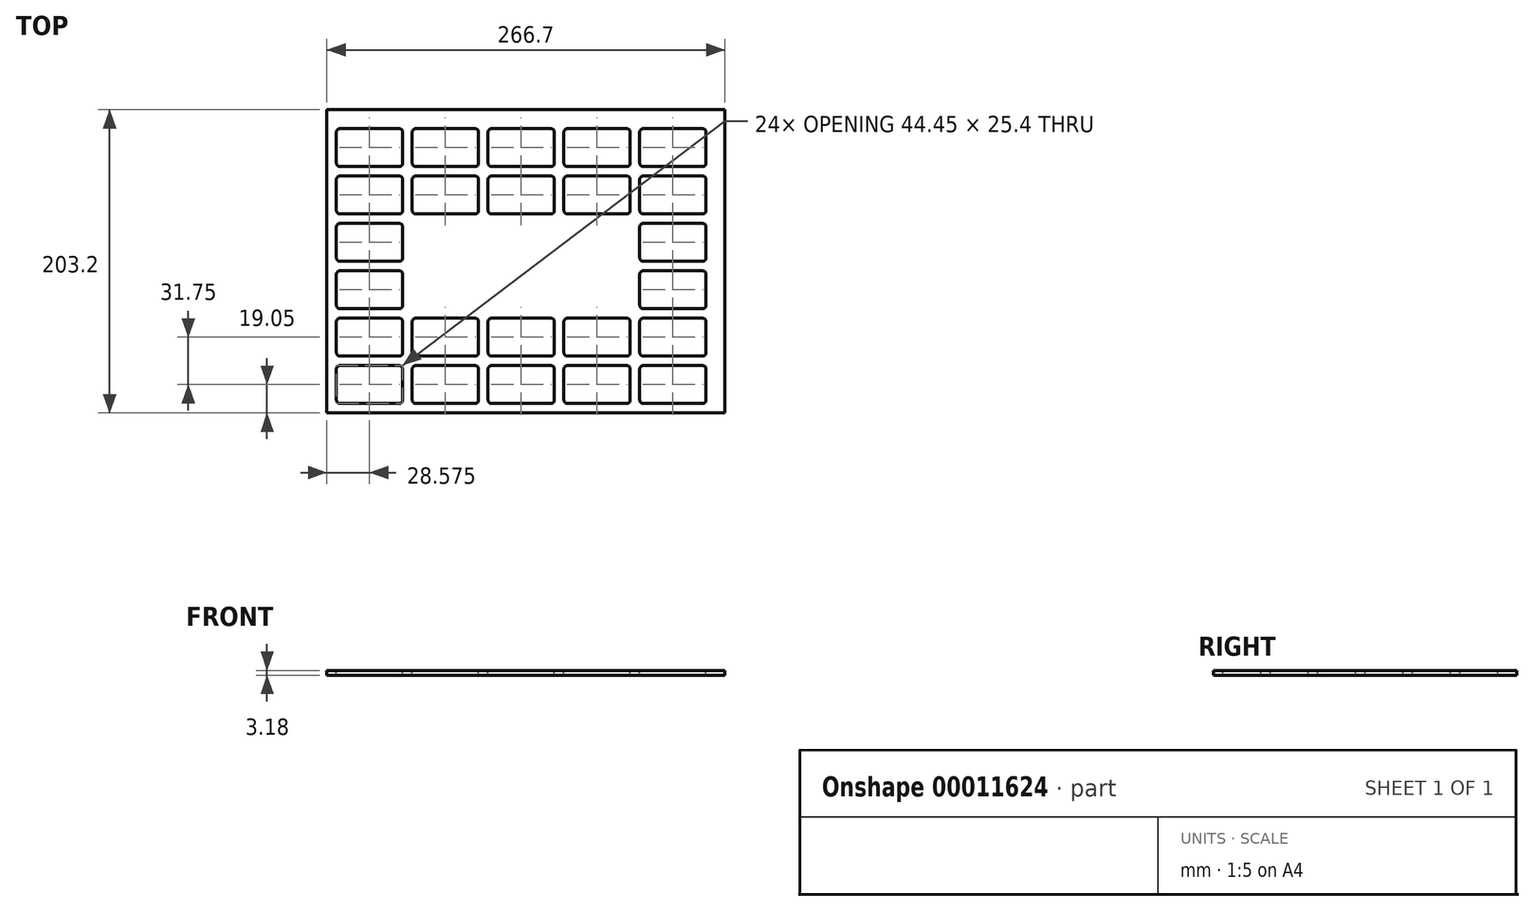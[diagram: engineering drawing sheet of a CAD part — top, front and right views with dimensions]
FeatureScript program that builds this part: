
annotation { "Feature Type Name" : "Feature", "Feature Type Description" : "" }
export const myFeature = defineFeature(function(context is Context, id is Id, definition is map)
    precondition{}
    {
        {
            var Q0;
            Q0=qCreatedBy(makeId("Top.planeOp"),FACE);
            var sketch = newSketch(context, id + "F0", { "sketchPlane" : qUnion([Q0])});
            skLineSegment(sketch, "E0.bottom", {"start": v(0, 0) * mm, "end": v(266.7, 0) * mm});
            skLineSegment(sketch, "E0.top", {"start": v(0, 203.2) * mm, "end": v(266.7, 203.2) * mm});
            skLineSegment(sketch, "E0.left", {"start": v(0, 0) * mm, "end": v(0, 203.2) * mm});
            skLineSegment(sketch, "E0.right", {"start": v(266.7, 0) * mm, "end": v(266.7, 203.2) * mm});
            skSolve(sketch);
        }
        {
            var Q0;
            Q0 = qSketchRegion(id + "F0", true);
            extrude(context, id + "F1", {"entities" : qUnion([Q0]), "oppositeDirection" : true, "depth" : 3.17 * mm});
        }
        {
            var Q0;
            Q0=makeQuery(id+"F0.imprint","IMPRINT",FACE,{"disambiguationData":[TD([[makeQuery(id+"F0.imprint","IMPRINT",EDGE,{"derivedFrom":sQuery(id+"F0.wireOp",EDGE,"E0.bottom")}),1.0]])]});
            var sketch = newSketch(context, id + "F2", { "sketchPlane" : qUnion([Q0])});
            skLineSegment(sketch, "E1.bottom", {"start": v(8.73, 6.35) * mm, "end": v(48.42, 6.35) * mm});
            skLineSegment(sketch, "E1.top", {"start": v(8.73, 31.75) * mm, "end": v(48.42, 31.75) * mm});
            skLineSegment(sketch, "E1.left", {"start": v(6.35, 8.73) * mm, "end": v(6.35, 29.37) * mm});
            skLineSegment(sketch, "E1.right", {"start": v(50.8, 8.73) * mm, "end": v(50.8, 29.37) * mm});
            skPoint(sketch, "E2.visualSharp", {"position": v(50.8, 31.75) * mm});
            skArc(sketch, "E2.filletArc", {"start": v(50.8, 29.37) * mm, "mid": v(50.1, 31.05) * mm, "end": v(48.42, 31.75) * mm});
            skPoint(sketch, "E3.visualSharp", {"position": v(50.8, 6.35) * mm});
            skArc(sketch, "E3.filletArc", {"start": v(48.42, 6.35) * mm, "mid": v(50.1, 7.05) * mm, "end": v(50.8, 8.73) * mm});
            skPoint(sketch, "E4.visualSharp", {"position": v(6.35, 6.35) * mm});
            skArc(sketch, "E4.filletArc", {"start": v(6.35, 8.73) * mm, "mid": v(7.05, 7.05) * mm, "end": v(8.73, 6.35) * mm});
            skPoint(sketch, "E5.visualSharp", {"position": v(6.35, 31.75) * mm});
            skArc(sketch, "E5.filletArc", {"start": v(8.73, 31.75) * mm, "mid": v(7.05, 31.05) * mm, "end": v(6.35, 29.37) * mm});
            skLineSegment(sketch, "E6.0.1.0", {"start": v(8.73, 63.5) * mm, "end": v(48.42, 63.5) * mm});
            skLineSegment(sketch, "E6.0.1.1", {"start": v(6.35, 40.48) * mm, "end": v(6.35, 61.12) * mm});
            skLineSegment(sketch, "E6.0.1.2", {"start": v(50.8, 40.48) * mm, "end": v(50.8, 61.12) * mm});
            skPoint(sketch, "E6.0.1.3", {"position": v(50.8, 63.5) * mm});
            skPoint(sketch, "E6.0.1.4", {"position": v(6.35, 38.1) * mm});
            skPoint(sketch, "E6.0.1.5", {"position": v(6.35, 63.5) * mm});
            skLineSegment(sketch, "E6.0.1.6", {"start": v(8.73, 38.1) * mm, "end": v(48.42, 38.1) * mm});
            skArc(sketch, "E6.0.1.7", {"start": v(6.35, 40.48) * mm, "mid": v(7.05, 38.8) * mm, "end": v(8.73, 38.1) * mm});
            skArc(sketch, "E6.0.1.8", {"start": v(8.73, 63.5) * mm, "mid": v(7.05, 62.8) * mm, "end": v(6.35, 61.12) * mm});
            skArc(sketch, "E6.0.1.9", {"start": v(50.8, 61.12) * mm, "mid": v(50.1, 62.8) * mm, "end": v(48.42, 63.5) * mm});
            skPoint(sketch, "E6.0.1.10", {"position": v(50.8, 38.1) * mm});
            skArc(sketch, "E6.0.1.11", {"start": v(48.42, 38.1) * mm, "mid": v(50.1, 38.8) * mm, "end": v(50.8, 40.48) * mm});
            skLineSegment(sketch, "E6.0.2.0", {"start": v(8.73, 95.25) * mm, "end": v(48.42, 95.25) * mm});
            skLineSegment(sketch, "E6.0.2.1", {"start": v(6.35, 72.23) * mm, "end": v(6.35, 92.87) * mm});
            skLineSegment(sketch, "E6.0.2.2", {"start": v(50.8, 72.23) * mm, "end": v(50.8, 92.87) * mm});
            skPoint(sketch, "E6.0.2.4", {"position": v(6.35, 69.85) * mm});
            skPoint(sketch, "E6.0.2.5", {"position": v(6.35, 95.25) * mm});
            skLineSegment(sketch, "E6.0.2.6", {"start": v(8.73, 69.85) * mm, "end": v(48.42, 69.85) * mm});
            skArc(sketch, "E6.0.2.7", {"start": v(6.35, 72.23) * mm, "mid": v(7.05, 70.55) * mm, "end": v(8.73, 69.85) * mm});
            skArc(sketch, "E6.0.2.8", {"start": v(8.73, 95.25) * mm, "mid": v(7.05, 94.55) * mm, "end": v(6.35, 92.87) * mm});
            skArc(sketch, "E6.0.2.9", {"start": v(50.8, 92.87) * mm, "mid": v(50.1, 94.55) * mm, "end": v(48.42, 95.25) * mm});
            skArc(sketch, "E6.0.2.11", {"start": v(48.42, 69.85) * mm, "mid": v(50.1, 70.55) * mm, "end": v(50.8, 72.23) * mm});
            skLineSegment(sketch, "E6.0.3.0", {"start": v(8.73, 127) * mm, "end": v(48.42, 127) * mm});
            skLineSegment(sketch, "E6.0.3.1", {"start": v(6.35, 103.98) * mm, "end": v(6.35, 124.62) * mm});
            skLineSegment(sketch, "E6.0.3.2", {"start": v(50.8, 103.98) * mm, "end": v(50.8, 124.62) * mm});
            skPoint(sketch, "E6.0.3.4", {"position": v(6.35, 101.6) * mm});
            skPoint(sketch, "E6.0.3.5", {"position": v(6.35, 127) * mm});
            skLineSegment(sketch, "E6.0.3.6", {"start": v(8.73, 101.6) * mm, "end": v(48.42, 101.6) * mm});
            skArc(sketch, "E6.0.3.7", {"start": v(6.35, 103.98) * mm, "mid": v(7.05, 102.3) * mm, "end": v(8.73, 101.6) * mm});
            skArc(sketch, "E6.0.3.8", {"start": v(8.73, 127) * mm, "mid": v(7.05, 126.3) * mm, "end": v(6.35, 124.62) * mm});
            skArc(sketch, "E6.0.3.9", {"start": v(50.8, 124.62) * mm, "mid": v(50.1, 126.3) * mm, "end": v(48.42, 127) * mm});
            skArc(sketch, "E6.0.3.11", {"start": v(48.42, 101.6) * mm, "mid": v(50.1, 102.3) * mm, "end": v(50.8, 103.98) * mm});
            skLineSegment(sketch, "E6.0.4.0", {"start": v(8.73, 158.75) * mm, "end": v(48.42, 158.75) * mm});
            skLineSegment(sketch, "E6.0.4.1", {"start": v(6.35, 135.73) * mm, "end": v(6.35, 156.37) * mm});
            skLineSegment(sketch, "E6.0.4.2", {"start": v(50.8, 135.73) * mm, "end": v(50.8, 156.37) * mm});
            skPoint(sketch, "E6.0.4.3", {"position": v(50.8, 158.75) * mm});
            skPoint(sketch, "E6.0.4.4", {"position": v(6.35, 133.35) * mm});
            skPoint(sketch, "E6.0.4.5", {"position": v(6.35, 158.75) * mm});
            skLineSegment(sketch, "E6.0.4.6", {"start": v(8.73, 133.35) * mm, "end": v(48.42, 133.35) * mm});
            skArc(sketch, "E6.0.4.7", {"start": v(6.35, 135.73) * mm, "mid": v(7.05, 134.05) * mm, "end": v(8.73, 133.35) * mm});
            skArc(sketch, "E6.0.4.8", {"start": v(8.73, 158.75) * mm, "mid": v(7.05, 158.05) * mm, "end": v(6.35, 156.37) * mm});
            skArc(sketch, "E6.0.4.9", {"start": v(50.8, 156.37) * mm, "mid": v(50.1, 158.05) * mm, "end": v(48.42, 158.75) * mm});
            skArc(sketch, "E6.0.4.11", {"start": v(48.42, 133.35) * mm, "mid": v(50.1, 134.05) * mm, "end": v(50.8, 135.73) * mm});
            skLineSegment(sketch, "E6.0.5.0", {"start": v(8.73, 190.5) * mm, "end": v(48.42, 190.5) * mm});
            skLineSegment(sketch, "E6.0.5.1", {"start": v(6.35, 167.48) * mm, "end": v(6.35, 188.12) * mm});
            skLineSegment(sketch, "E6.0.5.2", {"start": v(50.8, 167.48) * mm, "end": v(50.8, 188.12) * mm});
            skPoint(sketch, "E6.0.5.3", {"position": v(50.8, 190.5) * mm});
            skPoint(sketch, "E6.0.5.4", {"position": v(6.35, 165.1) * mm});
            skPoint(sketch, "E6.0.5.5", {"position": v(6.35, 190.5) * mm});
            skLineSegment(sketch, "E6.0.5.6", {"start": v(8.73, 165.1) * mm, "end": v(48.42, 165.1) * mm});
            skArc(sketch, "E6.0.5.7", {"start": v(6.35, 167.48) * mm, "mid": v(7.05, 165.8) * mm, "end": v(8.73, 165.1) * mm});
            skArc(sketch, "E6.0.5.8", {"start": v(8.73, 190.5) * mm, "mid": v(7.05, 189.8) * mm, "end": v(6.35, 188.12) * mm});
            skArc(sketch, "E6.0.5.9", {"start": v(50.8, 188.12) * mm, "mid": v(50.1, 189.8) * mm, "end": v(48.42, 190.5) * mm});
            skPoint(sketch, "E6.0.5.10", {"position": v(50.8, 165.1) * mm});
            skArc(sketch, "E6.0.5.11", {"start": v(48.42, 165.1) * mm, "mid": v(50.1, 165.8) * mm, "end": v(50.8, 167.48) * mm});
            skLineSegment(sketch, "E6.1.0.0", {"start": v(59.53, 31.75) * mm, "end": v(99.22, 31.75) * mm});
            skLineSegment(sketch, "E6.1.0.1", {"start": v(57.15, 8.73) * mm, "end": v(57.15, 29.37) * mm});
            skLineSegment(sketch, "E6.1.0.2", {"start": v(101.6, 8.73) * mm, "end": v(101.6, 29.37) * mm});
            skPoint(sketch, "E6.1.0.3", {"position": v(101.6, 31.75) * mm});
            skPoint(sketch, "E6.1.0.4", {"position": v(57.15, 6.35) * mm});
            skPoint(sketch, "E6.1.0.5", {"position": v(57.15, 31.75) * mm});
            skLineSegment(sketch, "E6.1.0.6", {"start": v(59.53, 6.35) * mm, "end": v(99.22, 6.35) * mm});
            skArc(sketch, "E6.1.0.7", {"start": v(57.15, 8.73) * mm, "mid": v(57.85, 7.05) * mm, "end": v(59.53, 6.35) * mm});
            skArc(sketch, "E6.1.0.8", {"start": v(59.53, 31.75) * mm, "mid": v(57.85, 31.05) * mm, "end": v(57.15, 29.37) * mm});
            skArc(sketch, "E6.1.0.9", {"start": v(101.6, 29.37) * mm, "mid": v(100.9, 31.05) * mm, "end": v(99.22, 31.75) * mm});
            skPoint(sketch, "E6.1.0.10", {"position": v(101.6, 6.35) * mm});
            skArc(sketch, "E6.1.0.11", {"start": v(99.22, 6.35) * mm, "mid": v(100.9, 7.05) * mm, "end": v(101.6, 8.73) * mm});
            skLineSegment(sketch, "E6.1.1.0", {"start": v(59.53, 63.5) * mm, "end": v(99.22, 63.5) * mm});
            skLineSegment(sketch, "E6.1.1.1", {"start": v(57.15, 40.48) * mm, "end": v(57.15, 61.12) * mm});
            skLineSegment(sketch, "E6.1.1.2", {"start": v(101.6, 40.48) * mm, "end": v(101.6, 61.12) * mm});
            skPoint(sketch, "E6.1.1.3", {"position": v(101.6, 63.5) * mm});
            skPoint(sketch, "E6.1.1.4", {"position": v(57.15, 38.1) * mm});
            skPoint(sketch, "E6.1.1.5", {"position": v(57.15, 63.5) * mm});
            skLineSegment(sketch, "E6.1.1.6", {"start": v(59.53, 38.1) * mm, "end": v(99.22, 38.1) * mm});
            skArc(sketch, "E6.1.1.7", {"start": v(57.15, 40.48) * mm, "mid": v(57.85, 38.8) * mm, "end": v(59.53, 38.1) * mm});
            skArc(sketch, "E6.1.1.8", {"start": v(59.53, 63.5) * mm, "mid": v(57.85, 62.8) * mm, "end": v(57.15, 61.12) * mm});
            skArc(sketch, "E6.1.1.9", {"start": v(101.6, 61.12) * mm, "mid": v(100.9, 62.8) * mm, "end": v(99.22, 63.5) * mm});
            skPoint(sketch, "E6.1.1.10", {"position": v(101.6, 38.1) * mm});
            skArc(sketch, "E6.1.1.11", {"start": v(99.22, 38.1) * mm, "mid": v(100.9, 38.8) * mm, "end": v(101.6, 40.48) * mm});
            skLineSegment(sketch, "E6.1.4.0", {"start": v(59.53, 158.75) * mm, "end": v(99.22, 158.75) * mm});
            skLineSegment(sketch, "E6.1.4.1", {"start": v(57.15, 135.73) * mm, "end": v(57.15, 156.37) * mm});
            skLineSegment(sketch, "E6.1.4.2", {"start": v(101.6, 135.73) * mm, "end": v(101.6, 156.37) * mm});
            skPoint(sketch, "E6.1.4.3", {"position": v(101.6, 158.75) * mm});
            skPoint(sketch, "E6.1.4.5", {"position": v(57.15, 158.75) * mm});
            skLineSegment(sketch, "E6.1.4.6", {"start": v(59.53, 133.35) * mm, "end": v(99.22, 133.35) * mm});
            skArc(sketch, "E6.1.4.7", {"start": v(57.15, 135.73) * mm, "mid": v(57.85, 134.05) * mm, "end": v(59.53, 133.35) * mm});
            skArc(sketch, "E6.1.4.8", {"start": v(59.53, 158.75) * mm, "mid": v(57.85, 158.05) * mm, "end": v(57.15, 156.37) * mm});
            skArc(sketch, "E6.1.4.9", {"start": v(101.6, 156.37) * mm, "mid": v(100.9, 158.05) * mm, "end": v(99.22, 158.75) * mm});
            skArc(sketch, "E6.1.4.11", {"start": v(99.22, 133.35) * mm, "mid": v(100.9, 134.05) * mm, "end": v(101.6, 135.73) * mm});
            skLineSegment(sketch, "E6.1.5.0", {"start": v(59.53, 190.5) * mm, "end": v(99.22, 190.5) * mm});
            skLineSegment(sketch, "E6.1.5.1", {"start": v(57.15, 167.48) * mm, "end": v(57.15, 188.12) * mm});
            skLineSegment(sketch, "E6.1.5.2", {"start": v(101.6, 167.48) * mm, "end": v(101.6, 188.12) * mm});
            skPoint(sketch, "E6.1.5.3", {"position": v(101.6, 190.5) * mm});
            skPoint(sketch, "E6.1.5.4", {"position": v(57.15, 165.1) * mm});
            skPoint(sketch, "E6.1.5.5", {"position": v(57.15, 190.5) * mm});
            skLineSegment(sketch, "E6.1.5.6", {"start": v(59.53, 165.1) * mm, "end": v(99.22, 165.1) * mm});
            skArc(sketch, "E6.1.5.7", {"start": v(57.15, 167.48) * mm, "mid": v(57.85, 165.8) * mm, "end": v(59.53, 165.1) * mm});
            skArc(sketch, "E6.1.5.8", {"start": v(59.53, 190.5) * mm, "mid": v(57.85, 189.8) * mm, "end": v(57.15, 188.12) * mm});
            skArc(sketch, "E6.1.5.9", {"start": v(101.6, 188.12) * mm, "mid": v(100.9, 189.8) * mm, "end": v(99.22, 190.5) * mm});
            skPoint(sketch, "E6.1.5.10", {"position": v(101.6, 165.1) * mm});
            skArc(sketch, "E6.1.5.11", {"start": v(99.22, 165.1) * mm, "mid": v(100.9, 165.8) * mm, "end": v(101.6, 167.48) * mm});
            skLineSegment(sketch, "E6.2.0.0", {"start": v(110.33, 31.75) * mm, "end": v(150.02, 31.75) * mm});
            skLineSegment(sketch, "E6.2.0.1", {"start": v(107.95, 8.73) * mm, "end": v(107.95, 29.37) * mm});
            skLineSegment(sketch, "E6.2.0.2", {"start": v(152.4, 8.73) * mm, "end": v(152.4, 29.37) * mm});
            skPoint(sketch, "E6.2.0.3", {"position": v(152.4, 31.75) * mm});
            skPoint(sketch, "E6.2.0.4", {"position": v(107.95, 6.35) * mm});
            skPoint(sketch, "E6.2.0.5", {"position": v(107.95, 31.75) * mm});
            skLineSegment(sketch, "E6.2.0.6", {"start": v(110.33, 6.35) * mm, "end": v(150.02, 6.35) * mm});
            skArc(sketch, "E6.2.0.7", {"start": v(107.95, 8.73) * mm, "mid": v(108.65, 7.05) * mm, "end": v(110.33, 6.35) * mm});
            skArc(sketch, "E6.2.0.8", {"start": v(110.33, 31.75) * mm, "mid": v(108.65, 31.05) * mm, "end": v(107.95, 29.37) * mm});
            skArc(sketch, "E6.2.0.9", {"start": v(152.4, 29.37) * mm, "mid": v(151.7, 31.05) * mm, "end": v(150.02, 31.75) * mm});
            skPoint(sketch, "E6.2.0.10", {"position": v(152.4, 6.35) * mm});
            skArc(sketch, "E6.2.0.11", {"start": v(150.02, 6.35) * mm, "mid": v(151.7, 7.05) * mm, "end": v(152.4, 8.73) * mm});
            skLineSegment(sketch, "E6.2.1.0", {"start": v(110.33, 63.5) * mm, "end": v(150.02, 63.5) * mm});
            skLineSegment(sketch, "E6.2.1.1", {"start": v(107.95, 40.48) * mm, "end": v(107.95, 61.12) * mm});
            skLineSegment(sketch, "E6.2.1.2", {"start": v(152.4, 40.48) * mm, "end": v(152.4, 61.12) * mm});
            skPoint(sketch, "E6.2.1.3", {"position": v(152.4, 63.5) * mm});
            skPoint(sketch, "E6.2.1.4", {"position": v(107.95, 38.1) * mm});
            skPoint(sketch, "E6.2.1.5", {"position": v(107.95, 63.5) * mm});
            skLineSegment(sketch, "E6.2.1.6", {"start": v(110.33, 38.1) * mm, "end": v(150.02, 38.1) * mm});
            skArc(sketch, "E6.2.1.7", {"start": v(107.95, 40.48) * mm, "mid": v(108.65, 38.8) * mm, "end": v(110.33, 38.1) * mm});
            skArc(sketch, "E6.2.1.8", {"start": v(110.33, 63.5) * mm, "mid": v(108.65, 62.8) * mm, "end": v(107.95, 61.12) * mm});
            skArc(sketch, "E6.2.1.9", {"start": v(152.4, 61.12) * mm, "mid": v(151.7, 62.8) * mm, "end": v(150.02, 63.5) * mm});
            skPoint(sketch, "E6.2.1.10", {"position": v(152.4, 38.1) * mm});
            skArc(sketch, "E6.2.1.11", {"start": v(150.02, 38.1) * mm, "mid": v(151.7, 38.8) * mm, "end": v(152.4, 40.48) * mm});
            skLineSegment(sketch, "E6.2.4.0", {"start": v(110.33, 158.75) * mm, "end": v(150.02, 158.75) * mm});
            skLineSegment(sketch, "E6.2.4.1", {"start": v(107.95, 135.73) * mm, "end": v(107.95, 156.37) * mm});
            skLineSegment(sketch, "E6.2.4.2", {"start": v(152.4, 135.73) * mm, "end": v(152.4, 156.37) * mm});
            skPoint(sketch, "E6.2.4.3", {"position": v(152.4, 158.75) * mm});
            skPoint(sketch, "E6.2.4.5", {"position": v(107.95, 158.75) * mm});
            skLineSegment(sketch, "E6.2.4.6", {"start": v(110.33, 133.35) * mm, "end": v(150.02, 133.35) * mm});
            skArc(sketch, "E6.2.4.7", {"start": v(107.95, 135.73) * mm, "mid": v(108.65, 134.05) * mm, "end": v(110.33, 133.35) * mm});
            skArc(sketch, "E6.2.4.8", {"start": v(110.33, 158.75) * mm, "mid": v(108.65, 158.05) * mm, "end": v(107.95, 156.37) * mm});
            skArc(sketch, "E6.2.4.9", {"start": v(152.4, 156.37) * mm, "mid": v(151.7, 158.05) * mm, "end": v(150.02, 158.75) * mm});
            skArc(sketch, "E6.2.4.11", {"start": v(150.02, 133.35) * mm, "mid": v(151.7, 134.05) * mm, "end": v(152.4, 135.73) * mm});
            skLineSegment(sketch, "E6.2.5.0", {"start": v(110.33, 190.5) * mm, "end": v(150.02, 190.5) * mm});
            skLineSegment(sketch, "E6.2.5.1", {"start": v(107.95, 167.48) * mm, "end": v(107.95, 188.12) * mm});
            skLineSegment(sketch, "E6.2.5.2", {"start": v(152.4, 167.48) * mm, "end": v(152.4, 188.12) * mm});
            skPoint(sketch, "E6.2.5.3", {"position": v(152.4, 190.5) * mm});
            skPoint(sketch, "E6.2.5.4", {"position": v(107.95, 165.1) * mm});
            skPoint(sketch, "E6.2.5.5", {"position": v(107.95, 190.5) * mm});
            skLineSegment(sketch, "E6.2.5.6", {"start": v(110.33, 165.1) * mm, "end": v(150.02, 165.1) * mm});
            skArc(sketch, "E6.2.5.7", {"start": v(107.95, 167.48) * mm, "mid": v(108.65, 165.8) * mm, "end": v(110.33, 165.1) * mm});
            skArc(sketch, "E6.2.5.8", {"start": v(110.33, 190.5) * mm, "mid": v(108.65, 189.8) * mm, "end": v(107.95, 188.12) * mm});
            skArc(sketch, "E6.2.5.9", {"start": v(152.4, 188.12) * mm, "mid": v(151.7, 189.8) * mm, "end": v(150.02, 190.5) * mm});
            skPoint(sketch, "E6.2.5.10", {"position": v(152.4, 165.1) * mm});
            skArc(sketch, "E6.2.5.11", {"start": v(150.02, 165.1) * mm, "mid": v(151.7, 165.8) * mm, "end": v(152.4, 167.48) * mm});
            skLineSegment(sketch, "E6.3.0.0", {"start": v(161.13, 31.75) * mm, "end": v(200.82, 31.75) * mm});
            skLineSegment(sketch, "E6.3.0.1", {"start": v(158.75, 8.73) * mm, "end": v(158.75, 29.37) * mm});
            skLineSegment(sketch, "E6.3.0.2", {"start": v(203.2, 8.73) * mm, "end": v(203.2, 29.37) * mm});
            skPoint(sketch, "E6.3.0.3", {"position": v(203.2, 31.75) * mm});
            skPoint(sketch, "E6.3.0.4", {"position": v(158.75, 6.35) * mm});
            skPoint(sketch, "E6.3.0.5", {"position": v(158.75, 31.75) * mm});
            skLineSegment(sketch, "E6.3.0.6", {"start": v(161.13, 6.35) * mm, "end": v(200.82, 6.35) * mm});
            skArc(sketch, "E6.3.0.7", {"start": v(158.75, 8.73) * mm, "mid": v(159.45, 7.05) * mm, "end": v(161.13, 6.35) * mm});
            skArc(sketch, "E6.3.0.8", {"start": v(161.13, 31.75) * mm, "mid": v(159.45, 31.05) * mm, "end": v(158.75, 29.37) * mm});
            skArc(sketch, "E6.3.0.9", {"start": v(203.2, 29.37) * mm, "mid": v(202.5, 31.05) * mm, "end": v(200.82, 31.75) * mm});
            skPoint(sketch, "E6.3.0.10", {"position": v(203.2, 6.35) * mm});
            skArc(sketch, "E6.3.0.11", {"start": v(200.82, 6.35) * mm, "mid": v(202.5, 7.05) * mm, "end": v(203.2, 8.73) * mm});
            skLineSegment(sketch, "E6.3.1.0", {"start": v(161.13, 63.5) * mm, "end": v(200.82, 63.5) * mm});
            skLineSegment(sketch, "E6.3.1.1", {"start": v(158.75, 40.48) * mm, "end": v(158.75, 61.12) * mm});
            skLineSegment(sketch, "E6.3.1.2", {"start": v(203.2, 40.48) * mm, "end": v(203.2, 61.12) * mm});
            skPoint(sketch, "E6.3.1.3", {"position": v(203.2, 63.5) * mm});
            skPoint(sketch, "E6.3.1.4", {"position": v(158.75, 38.1) * mm});
            skPoint(sketch, "E6.3.1.5", {"position": v(158.75, 63.5) * mm});
            skLineSegment(sketch, "E6.3.1.6", {"start": v(161.13, 38.1) * mm, "end": v(200.82, 38.1) * mm});
            skArc(sketch, "E6.3.1.7", {"start": v(158.75, 40.48) * mm, "mid": v(159.45, 38.8) * mm, "end": v(161.13, 38.1) * mm});
            skArc(sketch, "E6.3.1.8", {"start": v(161.13, 63.5) * mm, "mid": v(159.45, 62.8) * mm, "end": v(158.75, 61.12) * mm});
            skArc(sketch, "E6.3.1.9", {"start": v(203.2, 61.12) * mm, "mid": v(202.5, 62.8) * mm, "end": v(200.82, 63.5) * mm});
            skPoint(sketch, "E6.3.1.10", {"position": v(203.2, 38.1) * mm});
            skArc(sketch, "E6.3.1.11", {"start": v(200.82, 38.1) * mm, "mid": v(202.5, 38.8) * mm, "end": v(203.2, 40.48) * mm});
            skLineSegment(sketch, "E6.3.4.0", {"start": v(161.13, 158.75) * mm, "end": v(200.82, 158.75) * mm});
            skLineSegment(sketch, "E6.3.4.1", {"start": v(158.75, 135.73) * mm, "end": v(158.75, 156.37) * mm});
            skLineSegment(sketch, "E6.3.4.2", {"start": v(203.2, 135.73) * mm, "end": v(203.2, 156.37) * mm});
            skPoint(sketch, "E6.3.4.3", {"position": v(203.2, 158.75) * mm});
            skPoint(sketch, "E6.3.4.5", {"position": v(158.75, 158.75) * mm});
            skLineSegment(sketch, "E6.3.4.6", {"start": v(161.13, 133.35) * mm, "end": v(200.82, 133.35) * mm});
            skArc(sketch, "E6.3.4.7", {"start": v(158.75, 135.73) * mm, "mid": v(159.45, 134.05) * mm, "end": v(161.13, 133.35) * mm});
            skArc(sketch, "E6.3.4.8", {"start": v(161.13, 158.75) * mm, "mid": v(159.45, 158.05) * mm, "end": v(158.75, 156.37) * mm});
            skArc(sketch, "E6.3.4.9", {"start": v(203.2, 156.37) * mm, "mid": v(202.5, 158.05) * mm, "end": v(200.82, 158.75) * mm});
            skArc(sketch, "E6.3.4.11", {"start": v(200.82, 133.35) * mm, "mid": v(202.5, 134.05) * mm, "end": v(203.2, 135.73) * mm});
            skLineSegment(sketch, "E6.3.5.0", {"start": v(161.13, 190.5) * mm, "end": v(200.82, 190.5) * mm});
            skLineSegment(sketch, "E6.3.5.1", {"start": v(158.75, 167.48) * mm, "end": v(158.75, 188.12) * mm});
            skLineSegment(sketch, "E6.3.5.2", {"start": v(203.2, 167.48) * mm, "end": v(203.2, 188.12) * mm});
            skPoint(sketch, "E6.3.5.3", {"position": v(203.2, 190.5) * mm});
            skPoint(sketch, "E6.3.5.4", {"position": v(158.75, 165.1) * mm});
            skPoint(sketch, "E6.3.5.5", {"position": v(158.75, 190.5) * mm});
            skLineSegment(sketch, "E6.3.5.6", {"start": v(161.13, 165.1) * mm, "end": v(200.82, 165.1) * mm});
            skArc(sketch, "E6.3.5.7", {"start": v(158.75, 167.48) * mm, "mid": v(159.45, 165.8) * mm, "end": v(161.13, 165.1) * mm});
            skArc(sketch, "E6.3.5.8", {"start": v(161.13, 190.5) * mm, "mid": v(159.45, 189.8) * mm, "end": v(158.75, 188.12) * mm});
            skArc(sketch, "E6.3.5.9", {"start": v(203.2, 188.12) * mm, "mid": v(202.5, 189.8) * mm, "end": v(200.82, 190.5) * mm});
            skPoint(sketch, "E6.3.5.10", {"position": v(203.2, 165.1) * mm});
            skArc(sketch, "E6.3.5.11", {"start": v(200.82, 165.1) * mm, "mid": v(202.5, 165.8) * mm, "end": v(203.2, 167.48) * mm});
            skLineSegment(sketch, "E6.4.0.0", {"start": v(211.93, 31.75) * mm, "end": v(251.62, 31.75) * mm});
            skLineSegment(sketch, "E6.4.0.1", {"start": v(209.55, 8.73) * mm, "end": v(209.55, 29.37) * mm});
            skLineSegment(sketch, "E6.4.0.2", {"start": v(254, 8.73) * mm, "end": v(254, 29.37) * mm});
            skPoint(sketch, "E6.4.0.3", {"position": v(254, 31.75) * mm});
            skPoint(sketch, "E6.4.0.4", {"position": v(209.55, 6.35) * mm});
            skPoint(sketch, "E6.4.0.5", {"position": v(209.55, 31.75) * mm});
            skLineSegment(sketch, "E6.4.0.6", {"start": v(211.93, 6.35) * mm, "end": v(251.62, 6.35) * mm});
            skArc(sketch, "E6.4.0.7", {"start": v(209.55, 8.73) * mm, "mid": v(210.25, 7.05) * mm, "end": v(211.93, 6.35) * mm});
            skArc(sketch, "E6.4.0.8", {"start": v(211.93, 31.75) * mm, "mid": v(210.25, 31.05) * mm, "end": v(209.55, 29.37) * mm});
            skArc(sketch, "E6.4.0.9", {"start": v(254, 29.37) * mm, "mid": v(253.3, 31.05) * mm, "end": v(251.62, 31.75) * mm});
            skPoint(sketch, "E6.4.0.10", {"position": v(254, 6.35) * mm});
            skArc(sketch, "E6.4.0.11", {"start": v(251.62, 6.35) * mm, "mid": v(253.3, 7.05) * mm, "end": v(254, 8.73) * mm});
            skLineSegment(sketch, "E6.4.1.0", {"start": v(211.93, 63.5) * mm, "end": v(251.62, 63.5) * mm});
            skLineSegment(sketch, "E6.4.1.1", {"start": v(209.55, 40.48) * mm, "end": v(209.55, 61.12) * mm});
            skLineSegment(sketch, "E6.4.1.2", {"start": v(254, 40.48) * mm, "end": v(254, 61.12) * mm});
            skPoint(sketch, "E6.4.1.3", {"position": v(254, 63.5) * mm});
            skPoint(sketch, "E6.4.1.4", {"position": v(209.55, 38.1) * mm});
            skPoint(sketch, "E6.4.1.5", {"position": v(209.55, 63.5) * mm});
            skLineSegment(sketch, "E6.4.1.6", {"start": v(211.93, 38.1) * mm, "end": v(251.62, 38.1) * mm});
            skArc(sketch, "E6.4.1.7", {"start": v(209.55, 40.48) * mm, "mid": v(210.25, 38.8) * mm, "end": v(211.93, 38.1) * mm});
            skArc(sketch, "E6.4.1.8", {"start": v(211.93, 63.5) * mm, "mid": v(210.25, 62.8) * mm, "end": v(209.55, 61.12) * mm});
            skArc(sketch, "E6.4.1.9", {"start": v(254, 61.12) * mm, "mid": v(253.3, 62.8) * mm, "end": v(251.62, 63.5) * mm});
            skPoint(sketch, "E6.4.1.10", {"position": v(254, 38.1) * mm});
            skArc(sketch, "E6.4.1.11", {"start": v(251.62, 38.1) * mm, "mid": v(253.3, 38.8) * mm, "end": v(254, 40.48) * mm});
            skLineSegment(sketch, "E6.4.2.0", {"start": v(211.93, 95.25) * mm, "end": v(251.62, 95.25) * mm});
            skLineSegment(sketch, "E6.4.2.1", {"start": v(209.55, 72.23) * mm, "end": v(209.55, 92.87) * mm});
            skLineSegment(sketch, "E6.4.2.2", {"start": v(254, 72.23) * mm, "end": v(254, 92.87) * mm});
            skPoint(sketch, "E6.4.2.3", {"position": v(254, 95.25) * mm});
            skPoint(sketch, "E6.4.2.4", {"position": v(209.55, 69.85) * mm});
            skPoint(sketch, "E6.4.2.5", {"position": v(209.55, 95.25) * mm});
            skLineSegment(sketch, "E6.4.2.6", {"start": v(211.93, 69.85) * mm, "end": v(251.62, 69.85) * mm});
            skArc(sketch, "E6.4.2.7", {"start": v(209.55, 72.23) * mm, "mid": v(210.25, 70.55) * mm, "end": v(211.93, 69.85) * mm});
            skArc(sketch, "E6.4.2.8", {"start": v(211.93, 95.25) * mm, "mid": v(210.25, 94.55) * mm, "end": v(209.55, 92.87) * mm});
            skArc(sketch, "E6.4.2.9", {"start": v(254, 92.87) * mm, "mid": v(253.3, 94.55) * mm, "end": v(251.62, 95.25) * mm});
            skPoint(sketch, "E6.4.2.10", {"position": v(254, 69.85) * mm});
            skArc(sketch, "E6.4.2.11", {"start": v(251.62, 69.85) * mm, "mid": v(253.3, 70.55) * mm, "end": v(254, 72.23) * mm});
            skLineSegment(sketch, "E6.4.3.0", {"start": v(211.93, 127) * mm, "end": v(251.62, 127) * mm});
            skLineSegment(sketch, "E6.4.3.1", {"start": v(209.55, 103.98) * mm, "end": v(209.55, 124.62) * mm});
            skLineSegment(sketch, "E6.4.3.2", {"start": v(254, 103.98) * mm, "end": v(254, 124.62) * mm});
            skPoint(sketch, "E6.4.3.3", {"position": v(254, 127) * mm});
            skPoint(sketch, "E6.4.3.4", {"position": v(209.55, 101.6) * mm});
            skPoint(sketch, "E6.4.3.5", {"position": v(209.55, 127) * mm});
            skLineSegment(sketch, "E6.4.3.6", {"start": v(211.93, 101.6) * mm, "end": v(251.62, 101.6) * mm});
            skArc(sketch, "E6.4.3.7", {"start": v(209.55, 103.98) * mm, "mid": v(210.25, 102.3) * mm, "end": v(211.93, 101.6) * mm});
            skArc(sketch, "E6.4.3.8", {"start": v(211.93, 127) * mm, "mid": v(210.25, 126.3) * mm, "end": v(209.55, 124.62) * mm});
            skArc(sketch, "E6.4.3.9", {"start": v(254, 124.62) * mm, "mid": v(253.3, 126.3) * mm, "end": v(251.62, 127) * mm});
            skPoint(sketch, "E6.4.3.10", {"position": v(254, 101.6) * mm});
            skArc(sketch, "E6.4.3.11", {"start": v(251.62, 101.6) * mm, "mid": v(253.3, 102.3) * mm, "end": v(254, 103.98) * mm});
            skLineSegment(sketch, "E6.4.4.0", {"start": v(211.93, 158.75) * mm, "end": v(251.62, 158.75) * mm});
            skLineSegment(sketch, "E6.4.4.1", {"start": v(209.55, 135.73) * mm, "end": v(209.55, 156.37) * mm});
            skLineSegment(sketch, "E6.4.4.2", {"start": v(254, 135.73) * mm, "end": v(254, 156.37) * mm});
            skPoint(sketch, "E6.4.4.3", {"position": v(254, 158.75) * mm});
            skPoint(sketch, "E6.4.4.4", {"position": v(209.55, 133.35) * mm});
            skPoint(sketch, "E6.4.4.5", {"position": v(209.55, 158.75) * mm});
            skLineSegment(sketch, "E6.4.4.6", {"start": v(211.93, 133.35) * mm, "end": v(251.62, 133.35) * mm});
            skArc(sketch, "E6.4.4.7", {"start": v(209.55, 135.73) * mm, "mid": v(210.25, 134.05) * mm, "end": v(211.93, 133.35) * mm});
            skArc(sketch, "E6.4.4.8", {"start": v(211.93, 158.75) * mm, "mid": v(210.25, 158.05) * mm, "end": v(209.55, 156.37) * mm});
            skArc(sketch, "E6.4.4.9", {"start": v(254, 156.37) * mm, "mid": v(253.3, 158.05) * mm, "end": v(251.62, 158.75) * mm});
            skPoint(sketch, "E6.4.4.10", {"position": v(254, 133.35) * mm});
            skArc(sketch, "E6.4.4.11", {"start": v(251.62, 133.35) * mm, "mid": v(253.3, 134.05) * mm, "end": v(254, 135.73) * mm});
            skLineSegment(sketch, "E6.4.5.0", {"start": v(211.93, 190.5) * mm, "end": v(251.62, 190.5) * mm});
            skLineSegment(sketch, "E6.4.5.1", {"start": v(209.55, 167.48) * mm, "end": v(209.55, 188.12) * mm});
            skLineSegment(sketch, "E6.4.5.2", {"start": v(254, 167.48) * mm, "end": v(254, 188.12) * mm});
            skPoint(sketch, "E6.4.5.3", {"position": v(254, 190.5) * mm});
            skPoint(sketch, "E6.4.5.4", {"position": v(209.55, 165.1) * mm});
            skPoint(sketch, "E6.4.5.5", {"position": v(209.55, 190.5) * mm});
            skLineSegment(sketch, "E6.4.5.6", {"start": v(211.93, 165.1) * mm, "end": v(251.62, 165.1) * mm});
            skArc(sketch, "E6.4.5.7", {"start": v(209.55, 167.48) * mm, "mid": v(210.25, 165.8) * mm, "end": v(211.93, 165.1) * mm});
            skArc(sketch, "E6.4.5.8", {"start": v(211.93, 190.5) * mm, "mid": v(210.25, 189.8) * mm, "end": v(209.55, 188.12) * mm});
            skArc(sketch, "E6.4.5.9", {"start": v(254, 188.12) * mm, "mid": v(253.3, 189.8) * mm, "end": v(251.62, 190.5) * mm});
            skPoint(sketch, "E6.4.5.10", {"position": v(254, 165.1) * mm});
            skArc(sketch, "E6.4.5.11", {"start": v(251.62, 165.1) * mm, "mid": v(253.3, 165.8) * mm, "end": v(254, 167.48) * mm});
            skLineSegment(sketch, "E6.direction1", {"start": v(6.35, 6.35) * mm, "end": v(57.15, 6.35) * mm, "construction": true});
            skLineSegment(sketch, "E6.direction2", {"start": v(6.35, 6.35) * mm, "end": v(6.35, 38.1) * mm, "construction": true});
            skSolve(sketch);
        }
        {
            var Q0;
            Q0 = qSketchRegion(id + "F2", true);
            extrude(context, id + "F3", {"entities" : qUnion([Q0]), "operationType" : NewBodyOperationType.REMOVE, "endBound" : BoundingType.THROUGH_ALL, "oppositeDirection" : true, "depth" : 25.4 * mm});
        }
    });
